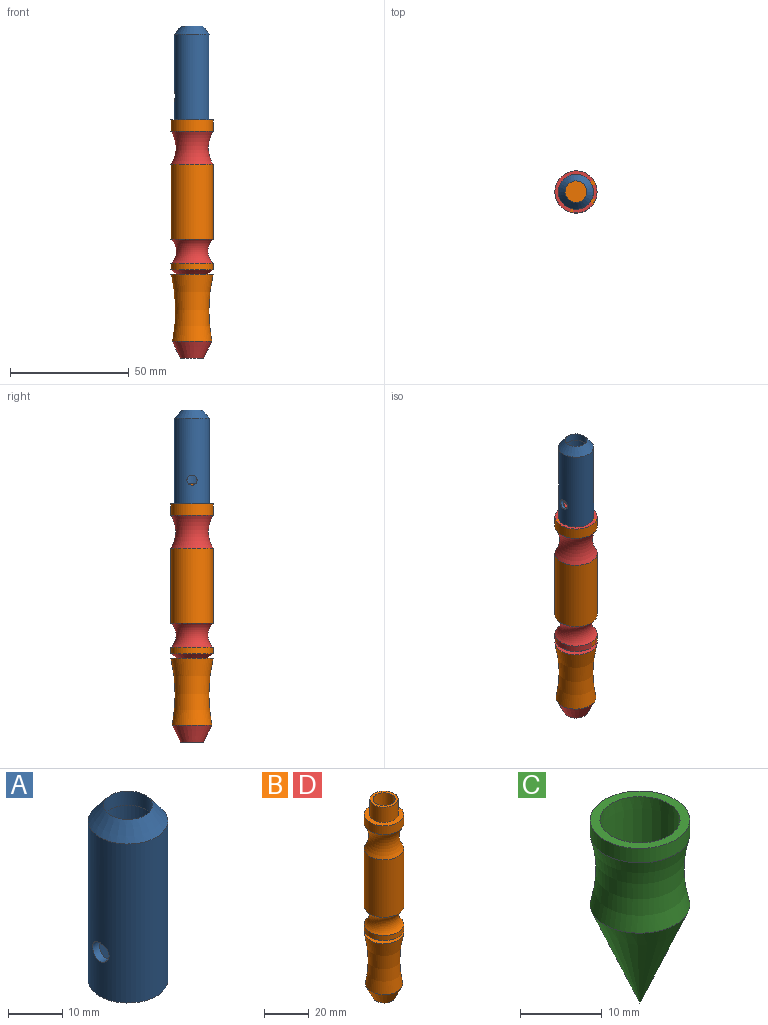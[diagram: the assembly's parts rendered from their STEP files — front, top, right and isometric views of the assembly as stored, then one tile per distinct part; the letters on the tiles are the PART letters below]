
ASSEMBLY  parts=4 mates=1
PART A: 7 faces, bbox 14.7x14.7x39.5 mm
  f0: cone r=3.68mm half-angle=38.4deg, axis (0,0,-1), area 169.9mm2, adj f3,f5
  f1: cylinder r=5.84mm len=36.25mm, axis (0,0,-1), area 1316.2mm2, adj f2,f4,f6
  f2: plane 14.73x14.73mm, normal (0,0,-1), area 63.2mm2, adj f1,f3
  f3: cylinder r=7.37mm len=35.91mm, axis (0,0,-1), area 1647.8mm2, adj f0,f2,f6
  f4: plane 11.68x11.68mm, normal (0,0,-1), area 42.3mm2, adj f1,f5
  f5: cylinder r=4.55mm len=9.09mm, axis (0,0,-1), area 92mm2, adj f0,f4
  f6: cylinder r=2.13mm len=4.25mm, axis (1,0,0), area 20.9mm2, adj f1,f3
PART B: 15 faces, bbox 56.9x56.9x135.4 mm
  f0: plane 9.91x9.91mm, normal (0,0,1), area 77.1mm2, adj f1
  f1: cylinder r=4.95mm len=73.16mm, axis (0,0,1), area 2276.9mm2, adj f0,f2
  f2: plane 12.64x12.64mm, normal (0,0,1), area 48.3mm2, adj f1,f3
  f3: cylinder r=6.32mm len=12.64mm, axis (0,0,1), area 333.7mm2, adj f2,f4
  f4: plane 17.72x17.72mm, normal (0,0,1), area 121.3mm2, adj f3,f5
  f5: cylinder r=8.86mm len=17.72mm, axis (0,0,1), area 268.1mm2, adj f4,f6
  f6: torus R=19.92mm, axis (0,0,1), area 693mm2, adj f5,f7
  f7: cylinder r=8.86mm len=31.54mm, axis (0,0,1), area 1755.9mm2, adj f6,f8
  f8: torus R=13.48mm, axis (0,0,1), area 523.3mm2, adj f7,f9
  f9: cylinder r=8.86mm len=17.72mm, axis (0,0,1), area 151.4mm2, adj f8,f10
  f10: cone r=6.6mm half-angle=51.3deg, axis (0,0,1), area 140.9mm2, adj f9,f11
  f11: plane 17.72x17.72mm, normal (0,0,1), area 109.9mm2, adj f10,f12
  f12: torus R=73.26mm, axis (0,0,1), area 1359.7mm2, adj f11,f13
  f13: cone r=4.92mm half-angle=26.1deg, axis (0,0,1), area 327.5mm2, adj f12,f14
  f14: plane 9.84x9.84mm, normal (0,0,-1), area 76mm2, adj f13
PART C: 6 faces, bbox 24x24x34 mm
  f0: cone r=0mm half-angle=22.4deg, axis (0,0,1), area 306.1mm2, adj f5
  f1: plane 9.91x9.91mm, normal (0,0,1), area 77.1mm2, adj f2
  f2: cone r=4.95mm half-angle=0.3deg, axis (0,0,-1), area 330.3mm2, adj f1,f3
  f3: plane 12.19x12.19mm, normal (0,0,1), area 41.3mm2, adj f2,f4
  f4: cylinder r=6.1mm len=12.19mm, axis (0,0,-1), area 83.1mm2, adj f3,f5
  f5: torus R=25.05mm, axis (0,0,-1), area 376.4mm2, adj f0,f4
PART D: same geometry as B
PLACE A t=(-118.48,-48.84,65.4)mm
PLACE B t=(-120.61,-48.84,34.4)mm
PLACE C t=(-118.48,-48.84,-7.23)mm
PLACE D t=(-120.61,-48.84,34.4)mm
MATE slider A.f0 <-> D.f6  axis (0,0,-1) through (-118.48,-48.84,65.4)mm
